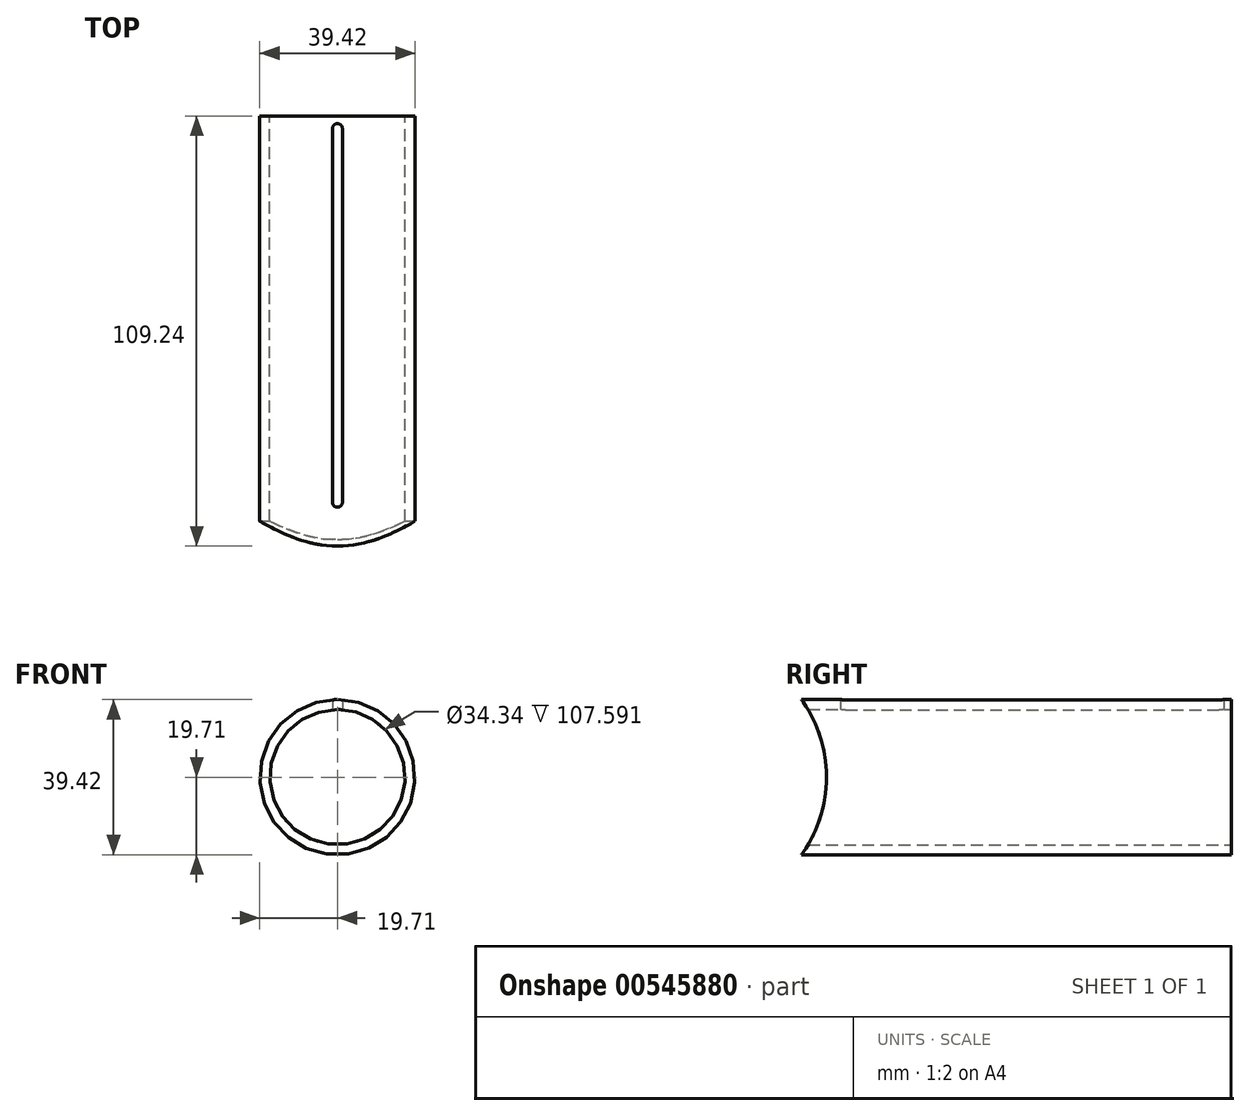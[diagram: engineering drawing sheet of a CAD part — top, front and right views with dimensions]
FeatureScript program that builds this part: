
annotation { "Feature Type Name" : "Feature", "Feature Type Description" : "" }
export const myFeature = defineFeature(function(context is Context, id is Id, definition is map)
    precondition{}
    {
        {
            var Q0;
            Q0=qCreatedBy(makeId("Front.planeOp"),FACE);
            var sketch = newSketch(context, id + "F0", { "sketchPlane" : qUnion([Q0])});
            skCircle(sketch, "E0", {"center": v(0, 0) * mm, "radius": 19.71 * mm});
            skCircle(sketch, "E1", {"center": v(0, 0) * mm, "radius": 17.17 * mm});
            skSolve(sketch);
        }
        {
            var Q0;
            Q0 = qSketchRegion(id + "F0", true);
            extrude(context, id + "F1", {"entities" : qUnion([Q0]), "endBound" : BoundingType.SYMMETRIC, "depth" : 114.3 * mm - 5.05 * mm, "offsetDistance" : 25.4 * mm});
        }
        {
            var Q0;
            Q0=qCreatedBy(makeId("Top.planeOp"),FACE);
            var sketch = newSketch(context, id + "F2", { "sketchPlane" : qUnion([Q0])});
            skLineSegment(sketch, "E2", {"start": v(-1.27, 51.45) * mm, "end": v(-1.27, -43.47) * mm});
            skArc(sketch, "E3", {"start": v(-1.27, 51.45) * mm, "mid": v(-0.9, 52.35) * mm, "end": v(0, 52.72) * mm});
            skArc(sketch, "E4", {"start": v(-1.27, -43.47) * mm, "mid": v(-0.9, -44.37) * mm, "end": v(0, -44.74) * mm});
            skArc(sketch, "E5.MirrorCS", {"start": v(1.27, 51.45) * mm, "mid": v(0.9, 52.35) * mm, "end": v(0, 52.72) * mm});
            skLineSegment(sketch, "E6.MirrorCS", {"start": v(1.27, 51.45) * mm, "end": v(1.27, -43.47) * mm});
            skArc(sketch, "E7.MirrorCS", {"start": v(1.27, -43.47) * mm, "mid": v(0.9, -44.37) * mm, "end": v(0, -44.74) * mm});
            skSolve(sketch);
        }
        {
            var Q0;
            Q0 = qSketchRegion(id + "F2", true);
            extrude(context, id + "F3", {"entities" : qUnion([Q0]), "operationType" : NewBodyOperationType.REMOVE, "endBound" : BoundingType.THROUGH_ALL, "depth" : 25.4 * mm, "offsetDistance" : 25.4 * mm});
        }
        {
            var Q0;
            Q0=qCreatedBy(makeId("Right.planeOp"),FACE);
            var sketch = newSketch(context, id + "F4", { "sketchPlane" : qUnion([Q0])});
            skLineSegment(sketch, "E8.0", {"start": v(-54.62, -19.71) * mm, "end": v(-54.62, 19.71) * mm});
            skCircle(sketch, "E9", {"center": v(-54.62, 0) * mm, "radius": 6.35 * mm, "construction": true});
            skArc(sketch, "E10", {"start": v(-54.62, -19.71) * mm, "mid": v(-48.27, 0) * mm, "end": v(-54.62, 19.71) * mm});
            skSolve(sketch);
        }
        {
            var Q0;
            Q0 = qSketchRegion(id + "F4", true);
            extrude(context, id + "F5", {"entities" : qUnion([Q0]), "operationType" : NewBodyOperationType.REMOVE, "endBound" : BoundingType.SYMMETRIC, "oppositeDirection" : true, "depth" : 50.8 * mm, "offsetDistance" : 25.4 * mm});
        }
    });
